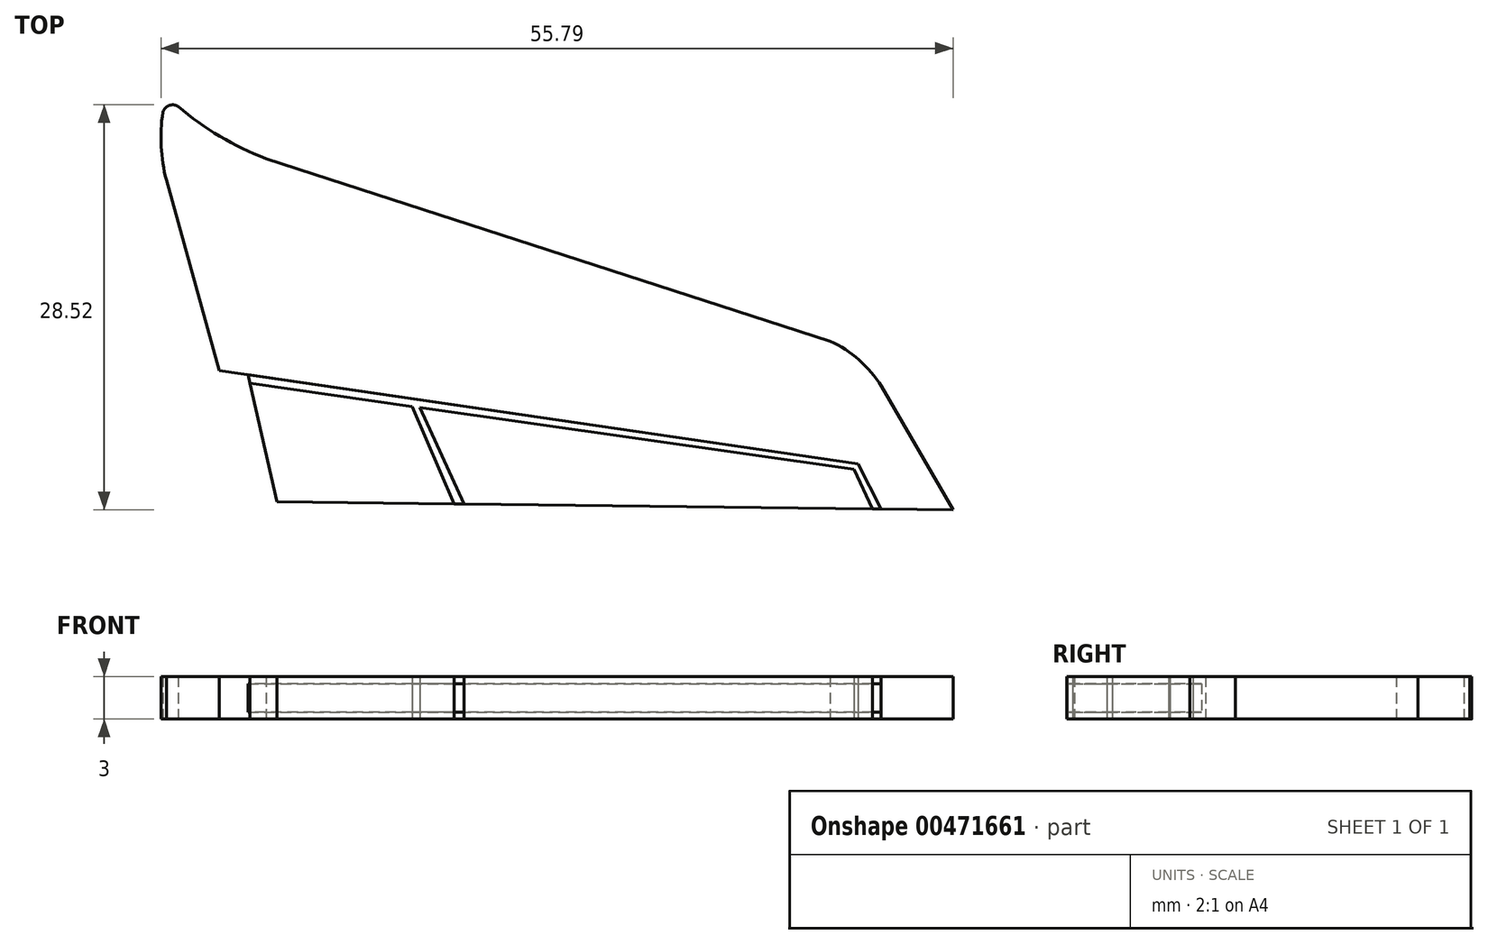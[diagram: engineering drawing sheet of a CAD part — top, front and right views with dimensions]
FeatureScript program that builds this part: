
annotation { "Feature Type Name" : "Feature", "Feature Type Description" : "" }
export const myFeature = defineFeature(function(context is Context, id is Id, definition is map)
    precondition{}
    {
        {
            var Q0;
            Q0=qCreatedBy(makeId("Top.planeOp"),FACE);
            var sketch = newSketch(context, id + "F0", { "sketchPlane" : qUnion([Q0])});
            skLineSegment(sketch, "E0", {"start": v(-29.54, -17.15) * mm, "end": v(-31.6, -8.2) * mm});
            skLineSegment(sketch, "E1", {"start": v(-29.54, -17.15) * mm, "end": v(18.06, -17.7) * mm});
            skLineSegment(sketch, "E2", {"start": v(18.06, -17.7) * mm, "end": v(11.58, -6.55) * mm});
            skLineSegment(sketch, "E3", {"start": v(11.58, -6.55) * mm, "end": v(-38.5, 9.67) * mm});
            skLineSegment(sketch, "E4", {"start": v(-38.5, 9.67) * mm, "end": v(-33.63, -7.91) * mm});
            skLineSegment(sketch, "E5", {"start": v(-33.63, -7.91) * mm, "end": v(11.38, -14.48) * mm});
            skLineSegment(sketch, "E6", {"start": v(11.38, -14.48) * mm, "end": v(13, -17.65) * mm});
            skLineSegment(sketch, "E7", {"start": v(12.4, -17.64) * mm, "end": v(11.1, -14.87) * mm});
            skLineSegment(sketch, "E8", {"start": v(11.1, -14.87) * mm, "end": v(-31.46, -8.81) * mm});
            skLineSegment(sketch, "E9", {"start": v(-17.08, -17.3) * mm, "end": v(-20.03, -10.44) * mm});
            skLineSegment(sketch, "E10", {"start": v(-16.39, -17.3) * mm, "end": v(-19.48, -10.52) * mm});
            skArc(sketch, "E11", {"start": v(13.02, -9.02) * mm, "mid": v(11.44, -7.16) * mm, "end": v(9.4, -5.84) * mm});
            skCircle(sketch, "E12", {"center": v(-36.9, 10.1) * mm, "radius": 0.71 * mm});
            skPoint(sketch, "E12.first.point", {"position": v(-37.6, 10.28) * mm});
            skPoint(sketch, "E12.second.point", {"position": v(-36.32, 10.5) * mm});
            skPoint(sketch, "E12.third.point", {"position": v(-36.33, 9.68) * mm});
            skArc(sketch, "E13", {"start": v(-36.51, 10.7) * mm, "mid": v(-33.58, 8.6) * mm, "end": v(-30.32, 7.03) * mm});
            skArc(sketch, "E14", {"start": v(-37.6, 10.28) * mm, "mid": v(-37.7, 7.71) * mm, "end": v(-37.25, 5.18) * mm});
            skLineSegment(sketch, "E15", {"start": v(-34.23, -5.74) * mm, "end": v(-35.94, -6.21) * mm});
            skLineSegment(sketch, "E16", {"start": v(-35.94, -6.21) * mm, "end": v(-40.68, 4.67) * mm});
            skLineSegment(sketch, "E17", {"start": v(-40.68, 4.67) * mm, "end": v(-37.55, 6.45) * mm});
            skLineSegment(sketch, "E18", {"start": v(-40.68, 4.67) * mm, "end": v(-41.42, 3.63) * mm});
            skLineSegment(sketch, "E19", {"start": v(-41.42, 3.63) * mm, "end": v(-37.11, -6.26) * mm});
            skLineSegment(sketch, "E20", {"start": v(-37.11, -6.26) * mm, "end": v(-35.94, -6.21) * mm});
            skSolve(sketch);
        }
        {
            var Q0;
            {var subQ0=sQuery(id+"F0.wireOp",EDGE,"E13");var subQ1=sQuery(id+"F0.wireOp",EDGE,"E12");var subQ2=makeQuery(id+"F0.imprint","INTERSECT",VERTEX,{"disambiguationData":[OD(0.0)],"derivedFrom":[subQ1,subQ0]});Q0=makeQuery(id+"F0.imprint","IMPRINT",FACE,{"disambiguationData":[TD([[makeQuery(id+"F0.imprint","IMPRINT",EDGE,{"disambiguationData":[TD([[subQ2,-1.0]])],"derivedFrom":subQ1}),1.0]])]});}
            var Q1;
            {var subQ0=sQuery(id+"F0.wireOp",EDGE,"E13");var subQ1=sQuery(id+"F0.wireOp",EDGE,"E3");var subQ2=makeQuery(id+"F0.imprint","INTERSECT",VERTEX,{"derivedFrom":[subQ1,subQ0]});Q1=makeQuery(id+"F0.imprint","IMPRINT",FACE,{"disambiguationData":[TD([[makeQuery(id+"F0.imprint","IMPRINT",EDGE,{"disambiguationData":[TD([[subQ2,-1.0]])],"derivedFrom":subQ1}),-1.0]])]});}
            var Q2;
            {var subQ0=sQuery(id+"F0.wireOp",EDGE,"E6");Q2=makeQuery(id+"F0.imprint","IMPRINT",FACE,{"disambiguationData":[TD([[makeQuery(id+"F0.imprint","IMPRINT",EDGE,{"derivedFrom":subQ0}),1.0]])]});}
            var Q3;
            {var subQ5=sQuery(id+"F0.wireOp",EDGE,"E9");Q3=makeQuery(id+"F0.imprint","IMPRINT",FACE,{"disambiguationData":[TD([[makeQuery(id+"F0.imprint","IMPRINT",EDGE,{"derivedFrom":subQ5}),1.0]])]});}
            var Q4;
            {var subQ0=sQuery(id+"F0.wireOp",EDGE,"E7");Q4=makeQuery(id+"F0.imprint","IMPRINT",FACE,{"disambiguationData":[TD([[makeQuery(id+"F0.imprint","IMPRINT",EDGE,{"derivedFrom":subQ0}),1.0]])]});}
            extrude(context, id + "F1", {"entities" : qUnion([Q0, Q1, Q2, Q3, Q4]), "depth" : 1.5 * mm, "offsetDistance" : 25 * mm, "hasSecondDirection" : true, "secondDirectionOppositeDirection" : true, "secondDirectionDepth" : 1.5 * mm});
        }
        {
            var Q0;
            {var subQ0=sQuery(id+"F0.wireOp",EDGE,"E9");Q0=makeQuery(id+"F0.imprint","IMPRINT",FACE,{"disambiguationData":[TD([[makeQuery(id+"F0.imprint","IMPRINT",EDGE,{"derivedFrom":subQ0}),-1.0]])]});}
            var Q1;
            {var subQ3=sQuery(id+"F0.wireOp",EDGE,"E6");Q1=makeQuery(id+"F0.imprint","IMPRINT",FACE,{"disambiguationData":[TD([[makeQuery(id+"F0.imprint","IMPRINT",EDGE,{"derivedFrom":subQ3}),-1.0]])]});}
            extrude(context, id + "F2", {"entities" : qUnion([Q0, Q1]), "depth" : 1 * mm, "offsetDistance" : 25 * mm, "hasSecondDirection" : true, "secondDirectionOppositeDirection" : true, "secondDirectionDepth" : 1 * mm});
        }
    });
